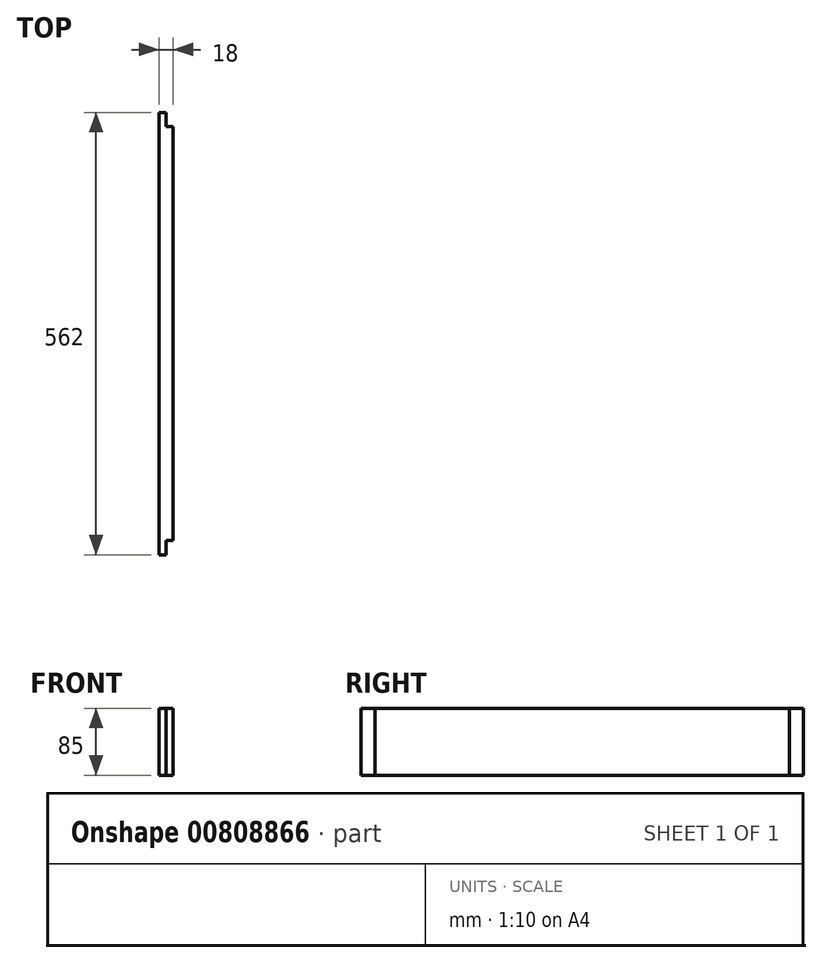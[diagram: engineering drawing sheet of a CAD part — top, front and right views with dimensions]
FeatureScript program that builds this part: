
annotation { "Feature Type Name" : "Feature", "Feature Type Description" : "" }
export const myFeature = defineFeature(function(context is Context, id is Id, definition is map)
    precondition{}
    {
        {
            var Q0;
            Q0=qCreatedBy(makeId("Right.planeOp"),FACE);
            var sketch = newSketch(context, id + "F0", { "sketchPlane" : qUnion([Q0])});
            skLineSegment(sketch, "E0.bottom", {"start": v(0, 0) * mm, "end": v(562, 0) * mm});
            skLineSegment(sketch, "E0.top", {"start": v(0, 85) * mm, "end": v(562, 85) * mm});
            skLineSegment(sketch, "E0.left", {"start": v(0, 0) * mm, "end": v(0, 85) * mm});
            skLineSegment(sketch, "E1.bottom", {"start": v(0, 85) * mm, "end": v(18, 85) * mm});
            skLineSegment(sketch, "E1.top", {"start": v(0, 0) * mm, "end": v(18, 0) * mm});
            skLineSegment(sketch, "E1.left", {"start": v(0, 85) * mm, "end": v(0, 0) * mm});
            skLineSegment(sketch, "E1.right", {"start": v(18, 85) * mm, "end": v(18, 0) * mm});
            skLineSegment(sketch, "E2.bottom", {"start": v(562, 85) * mm, "end": v(544, 85) * mm});
            skLineSegment(sketch, "E2.top", {"start": v(562, 0) * mm, "end": v(544, 0) * mm});
            skLineSegment(sketch, "E2.left", {"start": v(562, 85) * mm, "end": v(562, 0) * mm});
            skLineSegment(sketch, "E2.right", {"start": v(544, 85) * mm, "end": v(544, 0) * mm});
            skSolve(sketch);
        }
        {
            var Q0;
            {var subQ0=sQuery(id+"F0.wireOp",EDGE,"E1.right");Q0=makeQuery(id+"F0.imprint","IMPRINT",FACE,{"disambiguationData":[TD([[makeQuery(id+"F0.imprint","IMPRINT",EDGE,{"derivedFrom":subQ0}),1.0]])]});}
            extrude(context, id + "F1", {"entities" : qUnion([Q0]), "depth" : 18 * mm, "offsetDistance" : 25 * mm});
        }
        {
            var Q0;
            {var subQ2=sQuery(id+"F0.wireOp",EDGE,"E0.left");Q0=makeQuery(id+"F0.imprint","IMPRINT",FACE,{"disambiguationData":[TD([[makeQuery(id+"F0.imprint","IMPRINT",EDGE,{"derivedFrom":subQ2}),-1.0]])]});}
            var Q1;
            {var subQ0=sQuery(id+"F0.wireOp",EDGE,"E2.left");Q1=makeQuery(id+"F0.imprint","IMPRINT",FACE,{"disambiguationData":[TD([[makeQuery(id+"F0.imprint","IMPRINT",EDGE,{"derivedFrom":subQ0}),-1.0]])]});}
            extrude(context, id + "F2", {"entities" : qUnion([Q0, Q1]), "operationType" : NewBodyOperationType.ADD, "depth" : 9 * mm, "offsetDistance" : 25 * mm});
        }
    });
